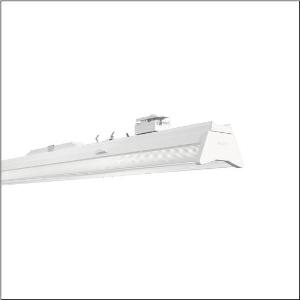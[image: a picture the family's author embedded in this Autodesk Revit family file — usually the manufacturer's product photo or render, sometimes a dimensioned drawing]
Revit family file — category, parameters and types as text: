
# Revit family: licross_r__11_performance_ho_51td16dn4fxm_21ba
name_source: partatom
category: Lighting Fixtures
units: mm (PartAtom-declared; Revit-internal decimal feet)

## family parameters
Cut with Voids When Loaded = No
Host = Face
Light Source = No
Part Type = Normal
Room Calculation Point = No
Round Connector Dimension = Use Diameter
Shared = No

## types (1)
- --- (1 x LED, 15460 lm, 87.3 W, 4000K)
    Apparent Load = 87 VA
    CIE Flux Codes = 63 87 95 78 100
    Color Rendering = 80
    Color Temperature = 4000K
    Default Elevation = 1800 mm
    Description = Licross® 11 Performance HO, luminaire insert, of sheet steel, galvanised, coil coated, white, length: 1.500mm, width: 120mm, height: 123mm, LED rated luminous flux: 15.460lm, light colour: 840, control gear: DALI 2, with plug, 5-pole, with phase selection, mains connection: 220..240V, AC, 50/60Hz, rated input power: 87W, halogen-free wiring, primary light control with lens, of plastic, primary optical cover: cover, of PMMA, light emission: direct/indirect distribution, primary light characteristic: symmetric, protection rating (complete): IP54, insulation class (complete): insulation class I (protective earthing), certification: CE, ENEC, VDE, UKCA, protection symbol: D if used in an environment with non-conductive dust loads with corresponding accessories, impact resistance: IK06, permissible ambient temperature for indoor applications: -25..+30°C, corresponds to IFS (International Featured Standards) requirements for safety and quality in the food industry, reducing of maximum allowable ambient temperature of 5°C with ceiling mounting, LABS conformity tested according to VDMA 24364:2018-05, packaging unit: 1 piece
    Height = 114 mm
    Lamp = 1 x LED
    Lamp Light Flux = 15460 lm
    Lamp Power = 87.3 W
    Lamp count = 1
    Length = 1500 mm
    Luminous efficacy = 177 lm/W
    Manufacturer = Siteco
    ModVariant = No
    Model = 51TD16DN4FXM
    Mounting Place = Ceiling
    Mounting Type = Pendant
    Number of Poles = 1
    OnlyDefault = Yes
    Power Factor = 1
    Product Name = Licross® 11 Performance HO
    Product group = luminaire insert
    ProductGroupID = 901
    Protection Class = Protection class I
    Protection Degree = IP 54
    RLX_Detail_Level = 1
    RLX_Emergency_Light_Flux = 0 lm
    RLX_Emergency_Type = 0
    RLX_Emergency_Type_DB = No
    RlxData = <blob elided: 34081 chars, md5=80568a07>
    Socket = socket
    Standby Power = 0 W
    System Light Flux = 15460 lm
    System Power = 87 W
    Type Comments = factory setting: luminous flux: 100 % | dim-lin: 254 | 589 mA
    Type Image = l_1256138.jpg
    URL = http://relux.com
    VarID = @adj_049635
    Voltage = 0 V
    Weight = 0.00 kg
    Width = 120 mm

## geometry (parser evidence)
native form markers: Blend x4, Sweep x12
no freeform markers — native parametric forms only
